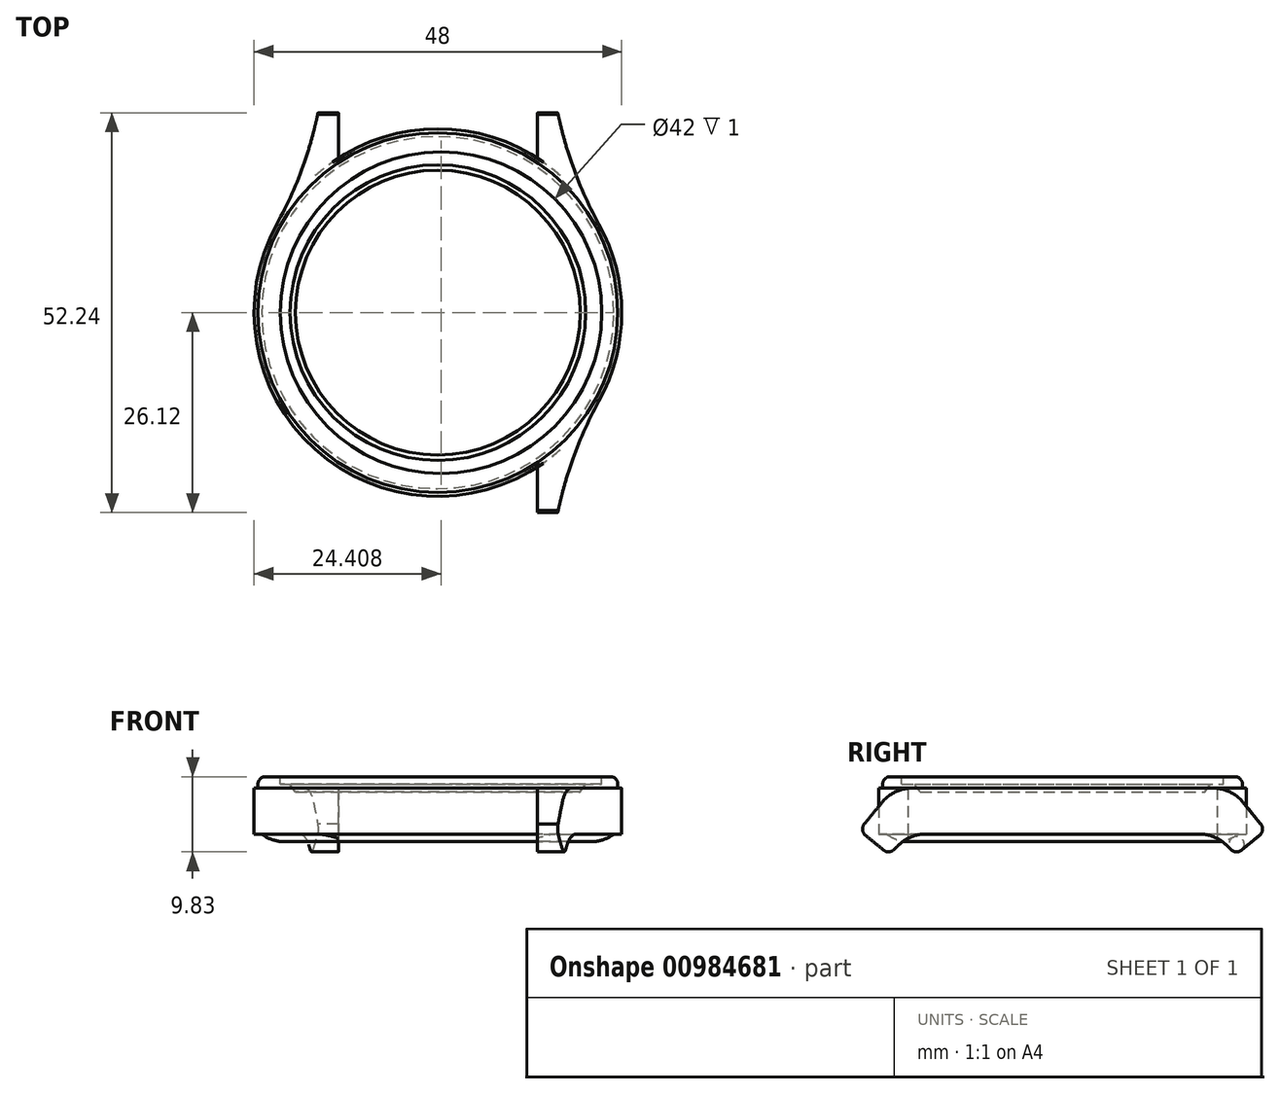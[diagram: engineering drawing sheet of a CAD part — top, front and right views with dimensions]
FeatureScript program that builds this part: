
annotation { "Feature Type Name" : "Feature", "Feature Type Description" : "" }
export const myFeature = defineFeature(function(context is Context, id is Id, definition is map)
    precondition{}
    {
        {
            var Q0;
            Q0=qCreatedBy(makeId("Top.planeOp"),FACE);
            var sketch = newSketch(context, id + "F0", { "sketchPlane" : qUnion([Q0])});
            skCircle(sketch, "E0", {"center": v(0, 0) * mm, "radius": 20 * mm});
            skSolve(sketch);
        }
        {
            var Q0;
            Q0=qCreatedBy(makeId("Top.planeOp"),FACE);
            var sketch = newSketch(context, id + "F1", { "sketchPlane" : qUnion([Q0])});
            skArc(sketch, "E1", {"start": v(0, 18) * mm, "mid": v(-12.73, 12.73) * mm, "end": v(-18, 0) * mm});
            skArc(sketch, "E2", {"start": v(0, 20) * mm, "mid": v(-14.14, 14.14) * mm, "end": v(-20, 0) * mm});
            skArc(sketch, "E3", {"start": v(0, 23.5) * mm, "mid": v(-16.62, 16.62) * mm, "end": v(-23.5, 0) * mm});
            skLineSegment(sketch, "E4", {"start": v(-13, 26.17) * mm, "end": v(-13, 20.17) * mm});
            skLineSegment(sketch, "E5", {"start": v(-13, 26.17) * mm, "end": v(-15.64, 26.17) * mm});
            skArc(sketch, "E6", {"start": v(0, 24) * mm, "mid": v(-16.97, 16.97) * mm, "end": v(-24, 0) * mm});
            skArc(sketch, "E7", {"start": v(-21.02, 11.58) * mm, "mid": v(-17.78, 18.67) * mm, "end": v(-15.64, 26.17) * mm});
            skLineSegment(sketch, "E8", {"start": v(-35.13, 0) * mm, "end": v(0, 0) * mm});
            skLineSegment(sketch, "E9", {"start": v(0, 0) * mm, "end": v(0, 30.2) * mm});
            skArc(sketch, "E10.MirrorCS", {"start": v(0, 24) * mm, "mid": v(16.97, 16.97) * mm, "end": v(24, 0) * mm});
            skArc(sketch, "E11.MirrorCS", {"start": v(0, 23.5) * mm, "mid": v(16.62, 16.62) * mm, "end": v(23.5, 0) * mm});
            skArc(sketch, "E12.MirrorCS", {"start": v(0, 20) * mm, "mid": v(14.14, 14.14) * mm, "end": v(20, 0) * mm});
            skArc(sketch, "E13.MirrorCS", {"start": v(0, 18) * mm, "mid": v(12.73, 12.73) * mm, "end": v(18, 0) * mm});
            skLineSegment(sketch, "E14.MirrorCS", {"start": v(13, 26.17) * mm, "end": v(13, 20.17) * mm});
            skLineSegment(sketch, "E15.MirrorCS", {"start": v(13, 26.17) * mm, "end": v(15.64, 26.17) * mm});
            skArc(sketch, "E16.MirrorCS", {"start": v(21.02, 11.58) * mm, "mid": v(17.78, 18.67) * mm, "end": v(15.64, 26.17) * mm});
            skLineSegment(sketch, "E17.MirrorCS", {"start": v(35.13, 0) * mm, "end": v(0, 0) * mm});
            skArc(sketch, "E18.MirrorCS", {"start": v(0, -18) * mm, "mid": v(-12.73, -12.73) * mm, "end": v(-18, 0) * mm});
            skArc(sketch, "E19.MirrorCS", {"start": v(0, -18) * mm, "mid": v(12.73, -12.73) * mm, "end": v(18, 0) * mm});
            skArc(sketch, "E20.MirrorCS", {"start": v(0, -20) * mm, "mid": v(14.14, -14.14) * mm, "end": v(20, 0) * mm});
            skArc(sketch, "E21.MirrorCS", {"start": v(0, -20) * mm, "mid": v(-14.14, -14.14) * mm, "end": v(-20, 0) * mm});
            skArc(sketch, "E22.MirrorCS", {"start": v(0, -23.5) * mm, "mid": v(-16.62, -16.62) * mm, "end": v(-23.5, 0) * mm});
            skArc(sketch, "E23.MirrorCS", {"start": v(0, -24) * mm, "mid": v(-16.97, -16.97) * mm, "end": v(-24, 0) * mm});
            skArc(sketch, "E24.MirrorCS", {"start": v(0, -24) * mm, "mid": v(16.97, -16.97) * mm, "end": v(24, 0) * mm});
            skArc(sketch, "E25.MirrorCS", {"start": v(0, -23.5) * mm, "mid": v(16.62, -16.62) * mm, "end": v(23.5, 0) * mm});
            skLineSegment(sketch, "E26.MirrorCS", {"start": v(13, -26.17) * mm, "end": v(13, -20.17) * mm});
            skLineSegment(sketch, "E27.MirrorCS", {"start": v(13, -26.17) * mm, "end": v(15.64, -26.17) * mm});
            skArc(sketch, "E28.MirrorCS", {"start": v(21.02, -11.58) * mm, "mid": v(17.78, -18.67) * mm, "end": v(15.64, -26.17) * mm});
            skLineSegment(sketch, "E29.MirrorCS", {"start": v(-13, -26.17) * mm, "end": v(-13, -20.17) * mm});
            skLineSegment(sketch, "E30.MirrorCS", {"start": v(-13, -26.17) * mm, "end": v(-15.64, -26.17) * mm});
            skArc(sketch, "E31.MirrorCS", {"start": v(-21.02, -11.58) * mm, "mid": v(-17.78, -18.67) * mm, "end": v(-15.64, -26.17) * mm});
            skSolve(sketch);
        }
        {
            var Q0;
            Q0=qCreatedBy(makeId("Top.planeOp"),FACE);
            var sketch = newSketch(context, id + "F2", { "sketchPlane" : qUnion([Q0])});
            skLineSegment(sketch, "E32.0", {"start": v(-13, 26.17) * mm, "end": v(-13, 20.17) * mm});
            skLineSegment(sketch, "E32.1", {"start": v(-13, 26.17) * mm, "end": v(-15.64, 26.17) * mm});
            skArc(sketch, "E32.2", {"start": v(-21.02, 11.58) * mm, "mid": v(-17.78, 18.67) * mm, "end": v(-15.64, 26.17) * mm});
            skLineSegment(sketch, "E32.4", {"start": v(13, 26.17) * mm, "end": v(13, 20.17) * mm});
            skLineSegment(sketch, "E33.MirrorCS", {"start": v(13, 26.17) * mm, "end": v(15.64, 26.17) * mm});
            skArc(sketch, "E34.MirrorCS", {"start": v(21.02, 11.58) * mm, "mid": v(17.78, 18.67) * mm, "end": v(15.64, 26.17) * mm});
            skArc(sketch, "E35.MirrorCS", {"start": v(-21.02, -11.58) * mm, "mid": v(-17.78, -18.67) * mm, "end": v(-15.64, -26.17) * mm});
            skLineSegment(sketch, "E36.MirrorCS", {"start": v(13, -26.17) * mm, "end": v(13, -20.17) * mm});
            skLineSegment(sketch, "E37.MirrorCS", {"start": v(13, -26.17) * mm, "end": v(15.64, -26.17) * mm});
            skArc(sketch, "E38.MirrorCS", {"start": v(21.02, -11.58) * mm, "mid": v(17.78, -18.67) * mm, "end": v(15.64, -26.17) * mm});
            skLineSegment(sketch, "E39.MirrorCS", {"start": v(-13, -26.17) * mm, "end": v(-15.64, -26.17) * mm});
            skLineSegment(sketch, "E40.MirrorCS", {"start": v(-13, -26.17) * mm, "end": v(-13, -20.17) * mm});
            skCircle(sketch, "E41", {"center": v(0, 0) * mm, "radius": 24 * mm});
            skSolve(sketch);
        }
        {
            var Q0;
            {var subQ0=sQuery(id+"F2.wireOp",EDGE,"E32.0");Q0=makeQuery(id+"F2.imprint","IMPRINT",FACE,{"disambiguationData":[TD([[makeQuery(id+"F2.imprint","IMPRINT",EDGE,{"derivedFrom":subQ0}),-1.0]])]});}
            var Q1;
            {var subQ0=sQuery(id+"F2.wireOp",EDGE,"E32.4");Q1=makeQuery(id+"F2.imprint","IMPRINT",FACE,{"disambiguationData":[TD([[makeQuery(id+"F2.imprint","IMPRINT",EDGE,{"derivedFrom":subQ0}),1.0]])]});}
            var Q2;
            {var subQ0=sQuery(id+"F2.wireOp",EDGE,"E35.MirrorCS");Q2=makeQuery(id+"F2.imprint","IMPRINT",FACE,{"disambiguationData":[TD([[makeQuery(id+"F2.imprint","IMPRINT",EDGE,{"derivedFrom":subQ0}),1.0]])]});}
            var Q3;
            {var subQ0=sQuery(id+"F2.wireOp",EDGE,"E36.MirrorCS");Q3=makeQuery(id+"F2.imprint","IMPRINT",FACE,{"disambiguationData":[TD([[makeQuery(id+"F2.imprint","IMPRINT",EDGE,{"derivedFrom":subQ0}),-1.0]])]});}
            extrude(context, id + "F3", {"entities" : qUnion([Q0, Q1, Q2, Q3]), "depth" : 25 * mm, "offsetDistance" : 25 * mm});
        }
        {
            var Q0;
            Q0=qCreatedBy(makeId("Right.planeOp"),FACE);
            var sketch = newSketch(context, id + "F4", { "sketchPlane" : qUnion([Q0])});
            skLineSegment(sketch, "E42", {"start": v(28.18, 0) * mm, "end": v(28.18, 7) * mm});
            skLineSegment(sketch, "E43", {"start": v(19.53, 3) * mm, "end": v(-24, 3) * mm});
            skLineSegment(sketch, "E44", {"start": v(25.78, 2.87) * mm, "end": v(23.37, 0.9) * mm});
            skLineSegment(sketch, "E45", {"start": v(22.04, 0.95) * mm, "end": v(21.35, 1.61) * mm});
            skPoint(sketch, "E46.newPointB", {"position": v(24, 3) * mm});
            skArc(sketch, "E46.filletArc", {"start": v(21.35, 1.61) * mm, "mid": v(19.75, 2.64) * mm, "end": v(17.9, 3) * mm});
            skLineSegment(sketch, "E47", {"start": v(25.92, 4.28) * mm, "end": v(23.55, 7.17) * mm});
            skLineSegment(sketch, "E48", {"start": v(19.68, 9) * mm, "end": v(8.53, 9) * mm});
            skPoint(sketch, "E49.visualSharp", {"position": v(23.68, 9) * mm});
            skArc(sketch, "E49.filletArc", {"start": v(23.55, 7.17) * mm, "mid": v(21.82, 8.52) * mm, "end": v(19.68, 9) * mm});
            skPoint(sketch, "E50.visualSharp", {"position": v(28.18, 3.5) * mm});
            skArc(sketch, "E50.filletArc", {"start": v(25.78, 2.87) * mm, "mid": v(26.14, 3.55) * mm, "end": v(25.92, 4.28) * mm});
            skPoint(sketch, "E51.visualSharp", {"position": v(22.68, 0.34) * mm});
            skArc(sketch, "E51.filletArc", {"start": v(22.04, 0.95) * mm, "mid": v(22.7, 0.67) * mm, "end": v(23.37, 0.9) * mm});
            skLineSegment(sketch, "E52", {"start": v(10.17, 9) * mm, "end": v(0, 9) * mm});
            skLineSegment(sketch, "E53", {"start": v(0, 9) * mm, "end": v(0, 3) * mm});
            skSolve(sketch);
        }
        {
            var Q0;
            Q0=qCreatedBy(makeId("Right.planeOp"),FACE);
            var sketch = newSketch(context, id + "F5", { "sketchPlane" : qUnion([Q0])});
            skLineSegment(sketch, "E54", {"start": v(27.8, 1.98) * mm, "end": v(23.55, 7.17) * mm});
            skLineSegment(sketch, "E55", {"start": v(19.68, 9) * mm, "end": v(-19.68, 9) * mm});
            skLineSegment(sketch, "E56", {"start": v(0, 9) * mm, "end": v(0, 1.4) * mm});
            skPoint(sketch, "E56.startSnap0", {"position": v(-0.4, 9) * mm});
            skPoint(sketch, "E57.newPointB", {"position": v(33.58, 9) * mm});
            skArc(sketch, "E57.filletArc", {"start": v(23.55, 7.17) * mm, "mid": v(21.82, 8.52) * mm, "end": v(19.68, 9) * mm});
            skLineSegment(sketch, "E58.MirrorCS", {"start": v(-19.68, 9) * mm, "end": v(19.68, 9) * mm});
            skArc(sketch, "E59.MirrorCS", {"start": v(-23.55, 7.17) * mm, "mid": v(-21.82, 8.52) * mm, "end": v(-19.68, 9) * mm});
            skLineSegment(sketch, "E60.MirrorCS", {"start": v(-27.8, 1.98) * mm, "end": v(-23.55, 7.17) * mm});
            skLineSegment(sketch, "E61.trimOffspring", {"start": v(33.58, 9) * mm, "end": v(34.38, 9) * mm});
            skPoint(sketch, "E62.orphan", {"position": v(-34.38, 9) * mm});
            skLineSegment(sketch, "E63", {"start": v(27.8, 1.98) * mm, "end": v(27.8, 26.74) * mm});
            skLineSegment(sketch, "E64", {"start": v(27.8, 26.74) * mm, "end": v(-29.06, 26.74) * mm});
            skLineSegment(sketch, "E65", {"start": v(-29.06, 26.74) * mm, "end": v(-27.8, 1.98) * mm});
            skSolve(sketch);
        }
        {
            var Q0;
            Q0=makeQuery(id+"F5.imprint","IMPRINT",FACE,{"disambiguationData":[TD([[makeQuery(id+"F5.imprint","IMPRINT",EDGE,{"derivedFrom":sQuery(id+"F5.wireOp",EDGE,"E54")}),-1.0]])]});
            extrude(context, id + "F6", {"entities" : qUnion([Q0]), "operationType" : NewBodyOperationType.REMOVE, "oppositeDirection" : true, "depth" : 25 * mm, "offsetDistance" : 25 * mm, "hasSecondDirection" : true, "secondDirectionOppositeDirection" : false, "secondDirectionDepth" : 25 * mm});
        }
        {
            var Q0;
            Q0=qCreatedBy(makeId("Right.planeOp"),FACE);
            var sketch = newSketch(context, id + "F7", { "sketchPlane" : qUnion([Q0])});
            skLineSegment(sketch, "E66", {"start": v(0, 3) * mm, "end": v(17.9, 3) * mm});
            skLineSegment(sketch, "E67", {"start": v(21.35, 1.61) * mm, "end": v(22.04, 0.95) * mm});
            skLineSegment(sketch, "E68", {"start": v(25.73, 2.83) * mm, "end": v(23.37, 0.9) * mm});
            skPoint(sketch, "E69.visualSharp", {"position": v(19.9, 3) * mm});
            skArc(sketch, "E69.filletArc", {"start": v(21.35, 1.61) * mm, "mid": v(19.75, 2.64) * mm, "end": v(17.9, 3) * mm});
            skArc(sketch, "E70.filletArc", {"start": v(22.04, 0.95) * mm, "mid": v(22.7, 0.67) * mm, "end": v(23.37, 0.9) * mm});
            skArc(sketch, "E71", {"start": v(25.73, 2.83) * mm, "mid": v(26.11, 3.55) * mm, "end": v(25.87, 4.34) * mm});
            skLineSegment(sketch, "E72", {"start": v(25.87, 4.34) * mm, "end": v(26.2, 4.5) * mm});
            skLineSegment(sketch, "E73", {"start": v(26.2, 4.5) * mm, "end": v(26.8, 3.23) * mm});
            skLineSegment(sketch, "E74", {"start": v(26.8, 3.23) * mm, "end": v(27.82, -2.26) * mm});
            skLineSegment(sketch, "E75", {"start": v(27.82, -2.26) * mm, "end": v(-28.11, -2.69) * mm});
            skLineSegment(sketch, "E76", {"start": v(-28.11, -2.69) * mm, "end": v(-28.5, 3.23) * mm});
            skLineSegment(sketch, "E77.MirrorCS", {"start": v(0, 3) * mm, "end": v(-17.9, 3) * mm});
            skArc(sketch, "E78.MirrorCS", {"start": v(-21.35, 1.61) * mm, "mid": v(-19.75, 2.64) * mm, "end": v(-17.9, 3) * mm});
            skLineSegment(sketch, "E79.MirrorCS", {"start": v(-25.73, 2.83) * mm, "end": v(-23.37, 0.9) * mm});
            skLineSegment(sketch, "E80.MirrorCS", {"start": v(-21.35, 1.61) * mm, "end": v(-22.04, 0.95) * mm});
            skArc(sketch, "E81.MirrorCS", {"start": v(-22.04, 0.95) * mm, "mid": v(-22.7, 0.67) * mm, "end": v(-23.37, 0.9) * mm});
            skArc(sketch, "E82.MirrorCS", {"start": v(-25.73, 2.83) * mm, "mid": v(-26.11, 3.55) * mm, "end": v(-25.87, 4.34) * mm});
            skLineSegment(sketch, "E83", {"start": v(-28.5, 3.23) * mm, "end": v(-26.69, 5.81) * mm});
            skLineSegment(sketch, "E84", {"start": v(-26.69, 5.81) * mm, "end": v(-25.87, 4.34) * mm});
            skSolve(sketch);
        }
        {
            var Q0;
            Q0=makeQuery(id+"F7.imprint","IMPRINT",FACE,{"disambiguationData":[TD([[makeQuery(id+"F7.imprint","IMPRINT",EDGE,{"derivedFrom":sQuery(id+"F7.wireOp",EDGE,"E66")}),-1.0]])]});
            extrude(context, id + "F8", {"entities" : qUnion([Q0]), "operationType" : NewBodyOperationType.REMOVE, "oppositeDirection" : true, "depth" : 25 * mm, "offsetDistance" : 25 * mm, "hasSecondDirection" : true, "secondDirectionOppositeDirection" : false, "secondDirectionDepth" : 25 * mm});
        }
        {
            var Q0;
            Q0=qCreatedBy(makeId("Top.planeOp"),FACE);
            var Q1;
            {var subQ0=sQuery(id+"F2.wireOp",EDGE,"E41");var subQ1=sQuery(id+"F2.wireOp",EDGE,"E32.2");Q1=makeQuery(id+"F8.boolean.opBoolean","INTERSECT",VERTEX,{"derivedFrom":[makeQuery(id+"F3.opExtrude","SWEPT_FACE",FACE,{"disambiguationData":[OSD([subQ1])]}),makeQuery(id+"F3.opExtrude","SWEPT_FACE",FACE,{"disambiguationData":[OSD([subQ0]),TDD([makeQuery(id+"F2.imprint","IMPRINT",EDGE,{"disambiguationData":[TD([[makeQuery(id+"F2.imprint","INTERSECT",VERTEX,{"derivedFrom":[sQuery(id+"F2.wireOp",EDGE,"E32.0"),subQ0]}),-1.0]])],"derivedFrom":subQ0})])]}),makeQuery(id+"F8.opExtrude","SWEPT_FACE",FACE,{"disambiguationData":[OSD([sQuery(id+"F7.wireOp",EDGE,"E66"),sQuery(id+"F7.wireOp",EDGE,"E77.MirrorCS")])]})]});}
            cPlane(context, id + "F9", {"entities" : qUnion([Q0, Q1]), "cplaneType" : CPlaneType.PLANE_POINT, "offset" : 25 * mm, "width" : 150 * mm, "height" : 150 * mm});
        }
        {
            var Q0;
            Q0=qCreatedBy(id+"F9.planeOp",FACE);
            var sketch = newSketch(context, id + "F10", { "sketchPlane" : qUnion([Q0])});
            skCircle(sketch, "E85", {"center": v(0, 0) * mm, "radius": 24 * mm});
            skSolve(sketch);
        }
        {
            var Q0;
            Q0 = qSketchRegion(id + "F10", true);
            extrude(context, id + "F11", {"entities" : qUnion([Q0]), "operationType" : NewBodyOperationType.ADD, "depth" : 6 * mm, "offsetDistance" : 25 * mm});
        }
        {
            var Q0;
            {var subQ0=sQuery(id+"F2.wireOp",EDGE,"E38.MirrorCS");var subQ3=makeQuery(id+"F8.opExtrude","SWEPT_FACE",FACE,{"disambiguationData":[OSD([sQuery(id+"F7.wireOp",EDGE,"E66"),sQuery(id+"F7.wireOp",EDGE,"E77.MirrorCS")])]});var subQ4=sQuery(id+"F2.wireOp",EDGE,"E35.MirrorCS");var subQ5=sQuery(id+"F2.wireOp",EDGE,"E34.MirrorCS");var subQ7=sQuery(id+"F2.wireOp",EDGE,"E32.2");Q0=makeQuery(id+"F11.boolean.opBoolean","MERGE",FACE,{"derivedFrom":[makeQuery(id+"F8.boolean.opBoolean","COPY",FACE,{"disambiguationData":[TD([makeQuery(id+"F3.opExtrude","SWEPT_FACE",FACE,{"disambiguationData":[OSD([subQ7])]})])],"derivedFrom":subQ3}),makeQuery(id+"F8.boolean.opBoolean","COPY",FACE,{"disambiguationData":[TD([makeQuery(id+"F3.opExtrude","SWEPT_FACE",FACE,{"disambiguationData":[OSD([subQ5])]})])],"derivedFrom":subQ3}),makeQuery(id+"F8.boolean.opBoolean","COPY",FACE,{"disambiguationData":[TD([makeQuery(id+"F3.opExtrude","SWEPT_FACE",FACE,{"disambiguationData":[OSD([subQ4])]})])],"derivedFrom":subQ3}),makeQuery(id+"F8.boolean.opBoolean","COPY",FACE,{"disambiguationData":[TD([makeQuery(id+"F3.opExtrude","SWEPT_FACE",FACE,{"disambiguationData":[OSD([subQ0])]})])],"derivedFrom":subQ3}),makeQuery(id+"F11.opExtrude","CAP_FACE",FACE,{"disambiguationData":[OSD([sQuery(id+"F10.wireOp",EDGE,"E85")])],"isStart":true})]});}
            var sketch = newSketch(context, id + "F12", { "sketchPlane" : qUnion([Q0])});
            skArc(sketch, "E86.0", {"start": v(0, 23) * mm, "mid": v(16.26, 16.26) * mm, "end": v(23, 0) * mm});
            skArc(sketch, "E86.1", {"start": v(0, 23) * mm, "mid": v(-16.26, 16.26) * mm, "end": v(-23, 0) * mm});
            skArc(sketch, "E86.2", {"start": v(0, -23) * mm, "mid": v(-16.26, -16.26) * mm, "end": v(-23, 0) * mm});
            skArc(sketch, "E86.3", {"start": v(0, -23) * mm, "mid": v(16.26, -16.26) * mm, "end": v(23, 0) * mm});
            skSolve(sketch);
        }
        {
            var Q0;
            Q0 = qSketchRegion(id + "F12", true);
            extrude(context, id + "F13", {"entities" : qUnion([Q0]), "operationType" : NewBodyOperationType.ADD, "depth" : 1 * mm, "offsetDistance" : 25 * mm});
        }
        {
            var Q0;
            Q0=makeQuery(id+"F13.opExtrude","CAP_EDGE",EDGE,{"disambiguationData":[OSD([sQuery(id+"F12.wireOp",EDGE,"E86.0"),sQuery(id+"F12.wireOp",EDGE,"E86.1"),sQuery(id+"F12.wireOp",EDGE,"E86.2"),sQuery(id+"F12.wireOp",EDGE,"E86.3")])],"isStart":false});
            fillet(context, id + "F14", {"entities" : qUnion([Q0]), "radius" : 5 * mm, "tangentPropagation" : true, "allowEdgeOverflow" : false});
        }
        {
            var Q0;
            {var subQ0=sQuery(id+"F2.wireOp",EDGE,"E38.MirrorCS");var subQ3=makeQuery(id+"F6.opExtrude","SWEPT_FACE",FACE,{"disambiguationData":[OSD([sQuery(id+"F5.wireOp",EDGE,"E58.MirrorCS")])]});var subQ4=sQuery(id+"F2.wireOp",EDGE,"E35.MirrorCS");var subQ5=sQuery(id+"F2.wireOp",EDGE,"E34.MirrorCS");var subQ7=sQuery(id+"F2.wireOp",EDGE,"E32.2");Q0=makeQuery(id+"F11.boolean.opBoolean","MERGE",FACE,{"derivedFrom":[makeQuery(id+"F6.boolean.opBoolean","COPY",FACE,{"disambiguationData":[TD([makeQuery(id+"F3.opExtrude","SWEPT_FACE",FACE,{"disambiguationData":[OSD([subQ7])]})])],"derivedFrom":subQ3}),makeQuery(id+"F6.boolean.opBoolean","COPY",FACE,{"disambiguationData":[TD([makeQuery(id+"F3.opExtrude","SWEPT_FACE",FACE,{"disambiguationData":[OSD([subQ5])]})])],"derivedFrom":subQ3}),makeQuery(id+"F6.boolean.opBoolean","COPY",FACE,{"disambiguationData":[TD([makeQuery(id+"F3.opExtrude","SWEPT_FACE",FACE,{"disambiguationData":[OSD([subQ4])]})])],"derivedFrom":subQ3}),makeQuery(id+"F6.boolean.opBoolean","COPY",FACE,{"disambiguationData":[TD([makeQuery(id+"F3.opExtrude","SWEPT_FACE",FACE,{"disambiguationData":[OSD([subQ0])]})])],"derivedFrom":subQ3}),makeQuery(id+"F11.opExtrude","CAP_FACE",FACE,{"disambiguationData":[OSD([sQuery(id+"F10.wireOp",EDGE,"E85")])],"isStart":false})]});}
            var sketch = newSketch(context, id + "F15", { "sketchPlane" : qUnion([Q0])});
            skCircle(sketch, "E87", {"center": v(0, 0) * mm, "radius": 23.5 * mm});
            skSolve(sketch);
        }
        {
            var Q0;
            Q0=makeQuery(id+"F15.imprint","IMPRINT",FACE,{"disambiguationData":[TD([[makeQuery(id+"F15.imprint","IMPRINT",EDGE,{"derivedFrom":sQuery(id+"F15.wireOp",EDGE,"E87")}),1.0]])]});
            extrude(context, id + "F16", {"entities" : qUnion([Q0]), "operationType" : NewBodyOperationType.ADD, "depth" : 1.5 * mm, "offsetDistance" : 25 * mm});
        }
        {
            var Q0;
            Q0=makeQuery(id+"F16.opExtrude","CAP_FACE",FACE,{"disambiguationData":[OSD([sQuery(id+"F15.wireOp",EDGE,"E87")])],"isStart":false});
            fillet(context, id + "F17", {"entities" : qUnion([Q0]), "radius" : 1 * mm, "tangentPropagation" : true, "allowEdgeOverflow" : false});
        }
        {
            var Q0;
            Q0=makeQuery(id+"F16.opExtrude","CAP_FACE",FACE,{"disambiguationData":[OSD([sQuery(id+"F15.wireOp",EDGE,"E87")])],"isStart":false});
            var sketch = newSketch(context, id + "F18", { "sketchPlane" : qUnion([Q0])});
            skCircle(sketch, "E88", {"center": v(0, 0) * mm, "radius": 20 * mm});
            skSolve(sketch);
        }
        {
            var Q0;
            Q0=makeQuery(id+"F18.imprint","IMPRINT",FACE,{"disambiguationData":[TD([[makeQuery(id+"F18.imprint","IMPRINT",EDGE,{"derivedFrom":sQuery(id+"F18.wireOp",EDGE,"E88")}),1.0]])]});
            extrude(context, id + "F19", {"entities" : qUnion([Q0]), "operationType" : NewBodyOperationType.REMOVE, "oppositeDirection" : true, "depth" : 2 * mm, "offsetDistance" : 25 * mm, "hasDraft" : true, "draftAngle" : 35 * degree, "draftPullDirection" : true});
        }
        {
            var Q0;
            Q0=makeQuery(id+"F16.opExtrude","CAP_FACE",FACE,{"disambiguationData":[OSD([sQuery(id+"F15.wireOp",EDGE,"E87")])],"isStart":false});
            var sketch = newSketch(context, id + "F20", { "sketchPlane" : qUnion([Q0])});
            skCircle(sketch, "E89", {"center": v(0.4, 0) * mm, "radius": 21 * mm});
            skSolve(sketch);
        }
        {
            var Q0;
            Q0 = qSketchRegion(id + "F20", true);
            extrude(context, id + "F21", {"entities" : qUnion([Q0]), "operationType" : NewBodyOperationType.REMOVE, "oppositeDirection" : true, "depth" : 1 * mm, "offsetDistance" : 25 * mm});
        }
    });
